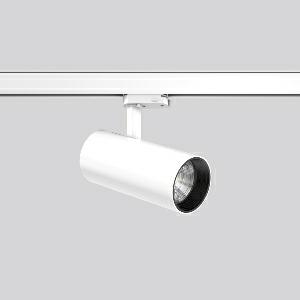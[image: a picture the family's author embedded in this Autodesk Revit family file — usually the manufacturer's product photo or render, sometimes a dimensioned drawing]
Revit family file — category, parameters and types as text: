
# Revit family: deecos_s_mini_742198_002_2_76_fbfb
name_source: partatom
category: Lighting Fixtures
units: mm (PartAtom-declared; Revit-internal decimal feet)

## family parameters
Cut with Voids When Loaded = No
Host = Face
Light Source = No
Part Type = Normal
Room Calculation Point = No
Round Connector Dimension = Use Diameter
Shared = No

## types (1)
- DEECOS S mini (1 x LED Modul 927, 2100 lm, 2700)
    Apparent Load = 20 VA
    Approval mark = CE
    CIE Flux Codes = 99 100 100 100 100
    Color Rendering = 92
    Color Temperature = 2700
    Default Elevation = 1800 mm
    Description = Series: DEECOS S mini
LED surface-mounted projector in modern design with no visible cooling ribs. Housing: die-cast aluminium, powder-coated. Rotation range: 356°. Swivel range: 90°. Black plastic ring and recessed LED to prevent glare from the side. Optical assembly with lens made of plastic (polycarbonate) for the best homogeneous light distribution - can be changed without tools. Best colour rendering index Ra>90. With adapter for RZB 3-circuit DALI tracks. Suitable for Track on ceiling, Wall track. High quality converter without flickering and stroboscopic effect. The following accessories can be mounted without use of tools: interchangeable lenses, decorative glasses, honeycomb louvre, clear and frosted diffusers, white interchangeable plastic ring. 
Colour: traffic white, matt (RAL 9016)
Diameter: 87 mm
Height: 214 mm
Lamp: LED
Socket: without socket
Colour temperature: 2700K
Colour rendering index (CRI): 92
System power: 20 W
Rated luminous flux: 2100 lm
Luminous efficiency: 105 lm/W
Control gear: Converter, dimmable, DALI
Protection class: I
Type of protection: IP 20
    Height = 214 mm
    Lamp = 1 x LED Modul 927
    Lamp Light Flux = 2100 lm
    Lamp count = 1
    Length = 87 mm
    Lifetime = 50000 h
    Luminous efficacy = 105 lm/W
    Manufacturer = RZB
    ModVariant = No
    Model = 742198.002.2.76
    Mounting Place = Ceiling
    Mounting Type = Rail mounted
    Number of Poles = 1
    OnlyDefault = Yes
    Power Factor = 1
    Product Name = DEECOS S mini
    Product group = Track mounted projectors
    ProductGroupID = 301
    Protection Class = Protection class I
    Protection Degree = IP 20
    RLX_Detail_Level = 1
    RLX_Emergency_Light_Flux = 0 lm
    RLX_Emergency_Type = 0
    RLX_Emergency_Type_DB = No
    RlxData = <blob elided: 34965 chars, md5=14188d21>
    Socket = socket
    Standby Power = 0 W
    System Light Flux = 2100 lm
    System Power = 20 W
    Type Comments = Product without accessories
    Type Image = 741930.002.jpg
    URL = http://relux.com
    VarID = ---
    Voltage = 230 V
    Voltage Range = 220-240 V
    Weight = 0.00 kg
    Width = 0 mm  [stored 0 ft]

note: [stored X ft] marks values corroborated as IEEE doubles in the binary element streams (Revit-internal decimal feet)

## geometry (parser evidence)
native form markers: Blend x4, Sweep x13
no freeform markers — native parametric forms only
